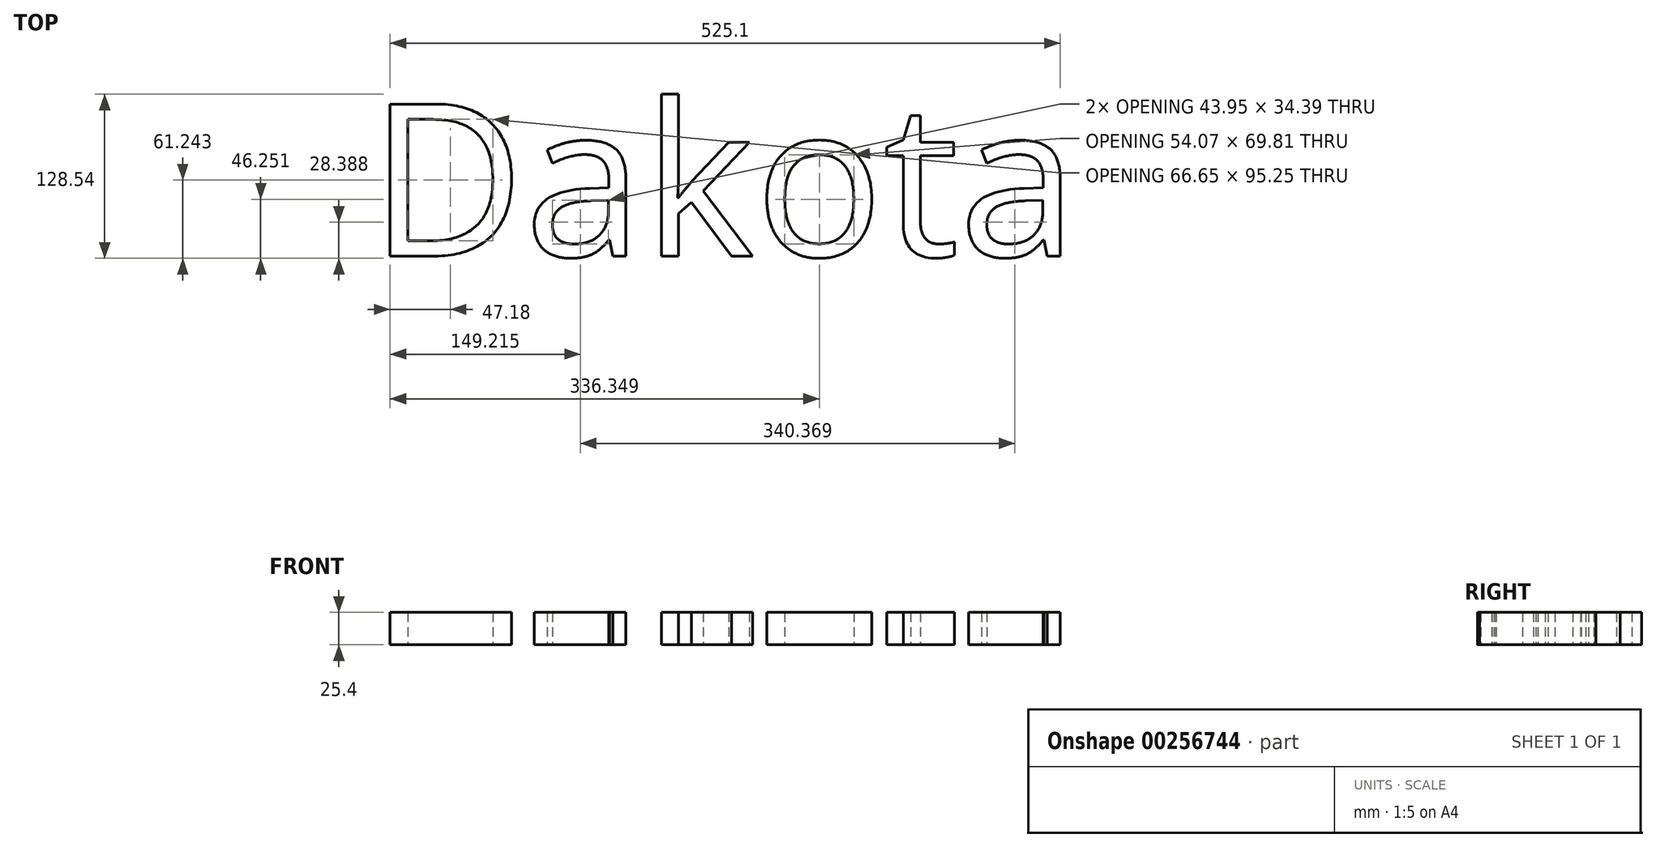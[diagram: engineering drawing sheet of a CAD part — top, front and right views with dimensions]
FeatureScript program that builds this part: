
annotation { "Feature Type Name" : "Feature", "Feature Type Description" : "" }
export const myFeature = defineFeature(function(context is Context, id is Id, definition is map)
    precondition{}
    {
        {
            var Q0;
            Q0=qCreatedBy(makeId("Top.planeOp"),FACE);
            var sketch = newSketch(context, id + "F0", { "sketchPlane" : qUnion([Q0])});
            skText(sketch, "E0", { "text": "Dakota", "fontName": "OpenSans-Regular.ttf"});
            const initialGuessF0  = {"E0": [-0.23433, -0.10913, 1, 0, 0.12025]};
            skSetInitialGuess(sketch, initialGuessF0);
            skSolve(sketch);
        }
        {
            var Q0;
            Q0 = qSketchRegion(id + "F0", true);
            extrude(context, id + "F1", {"entities" : qUnion([Q0]), "depth" : 25.4 * mm});
        }
    });
